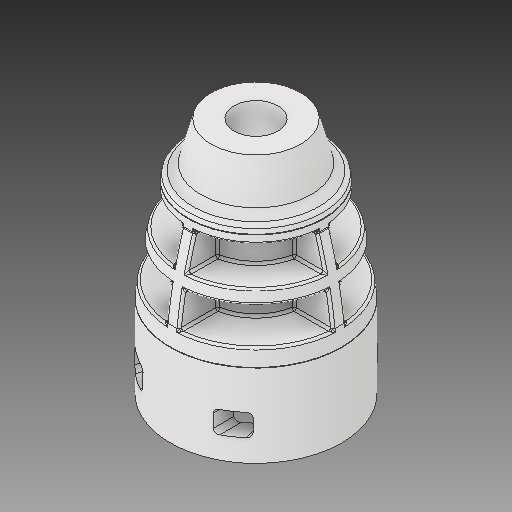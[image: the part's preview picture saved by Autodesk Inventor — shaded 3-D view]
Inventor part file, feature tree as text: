
AUTODESK INVENTOR PART (.ipt)
format: ipt  version: 2018 (Build 220112000, 112)  size: 835,072 bytes
history: native  units: in
note: dims shown in document units (in); Inventor stores cm internally (conversion verified against a paired STEP export)
features: fillet x1
ambient origin geometry x8: Origin, YZ Plane, XZ Plane, XY Plane, X Axis, Y Axis, Z Axis, Center Point
bodies: Solid1 (feature_tree)
feature tree (1):
  fillet  "Fillet3"  [1 undecoded]
note: 1 required parameter value undecoded (feature->parameter linkage not recoverable at this tier; creation-order binding heuristic only, values carry confidence <= 0.55)
